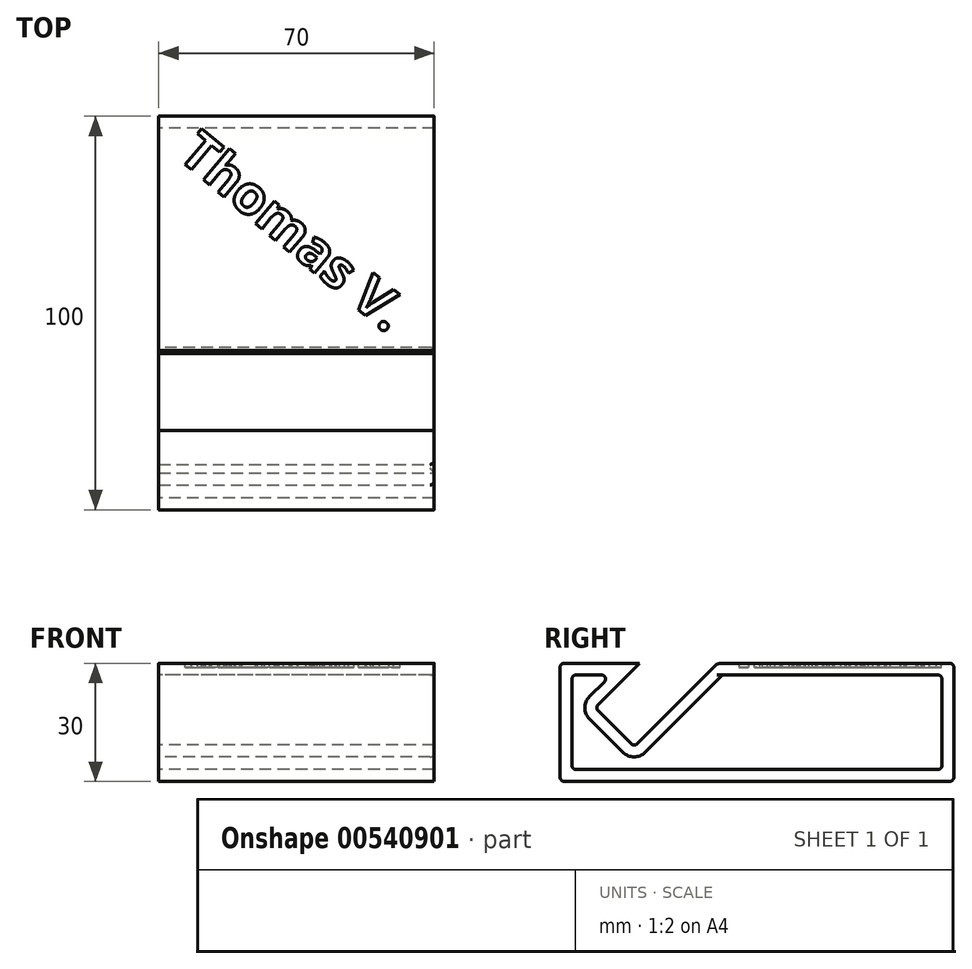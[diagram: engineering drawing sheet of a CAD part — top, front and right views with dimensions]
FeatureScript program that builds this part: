
annotation { "Feature Type Name" : "Feature", "Feature Type Description" : "" }
export const myFeature = defineFeature(function(context is Context, id is Id, definition is map)
    precondition{}
    {
        {
            var Q0;
            Q0=qCreatedBy(makeId("Top.planeOp"),FACE);
            var sketch = newSketch(context, id + "F0", { "sketchPlane" : qUnion([Q0])});
            skLineSegment(sketch, "E0.bottom", {"start": v(35, 50) * mm, "end": v(-35, 50) * mm});
            skLineSegment(sketch, "E0.top", {"start": v(35, -50) * mm, "end": v(-35, -50) * mm});
            skLineSegment(sketch, "E0.left", {"start": v(35, 50) * mm, "end": v(35, -50) * mm});
            skLineSegment(sketch, "E0.right", {"start": v(-35, 50) * mm, "end": v(-35, -50) * mm});
            skPoint(sketch, "E0.middle", {"position": v(0, 0) * mm});
            skSolve(sketch);
        }
        {
            var Q0;
            Q0 = qSketchRegion(id + "F0", true);
            extrude(context, id + "F1", {"entities" : qUnion([Q0]), "depth" : 30 * mm, "offsetDistance" : 25 * mm});
        }
        {
            var Q0;
            Q0=makeQuery(id+"F1.opExtrude","SWEPT_FACE",FACE,{"disambiguationData":[OSD([sQuery(id+"F0.wireOp",EDGE,"E0.left")])]});
            var sketch = newSketch(context, id + "F2", { "sketchPlane" : qUnion([Q0])});
            skLineSegment(sketch, "E1.bottom", {"start": v(-10, 30) * mm, "end": v(-31.21, 8.79) * mm});
            skLineSegment(sketch, "E1.top", {"start": v(-19.9, 39.9) * mm, "end": v(-41.11, 18.69) * mm});
            skLineSegment(sketch, "E1.left", {"start": v(-10, 30) * mm, "end": v(-19.9, 39.9) * mm});
            skLineSegment(sketch, "E1.right", {"start": v(-31.21, 8.79) * mm, "end": v(-41.11, 18.69) * mm});
            skPoint(sketch, "E2.firstSnap0", {"position": v(-20.6, 19.4) * mm});
            skSolve(sketch);
        }
        {
            var Q0;
            {var subQ0=sQuery(id+"F2.wireOp",EDGE,"E1.bottom");Q0=makeQuery(id+"F2.imprint","IMPRINT",FACE,{"disambiguationData":[TD([[makeQuery(id+"F2.imprint","IMPRINT",EDGE,{"derivedFrom":subQ0}),-1.0]])]});}
            extrude(context, id + "F3", {"entities" : qUnion([Q0]), "operationType" : NewBodyOperationType.REMOVE, "oppositeDirection" : true, "depth" : 146 * mm, "offsetDistance" : 25 * mm});
        }
        {
            var Q0;
            Q0=makeQuery(id+"F3.boolean.opBoolean","COPY",EDGE,{"derivedFrom":makeQuery(id+"F3.opExtrude","SWEPT_EDGE",EDGE,{"disambiguationData":[OSD([sQuery(id+"F0.wireOp",EDGE,"E0.left"),sQuery(id+"F2.wireOp",EDGE,"E1.top")])]})});
            var Q1;
            Q1=makeQuery(id+"F3.boolean.opBoolean","COPY",EDGE,{"derivedFrom":makeQuery(id+"F3.opExtrude","SWEPT_EDGE",EDGE,{"disambiguationData":[OSD([sQuery(id+"F2.wireOp",EDGE,"E1.top"),sQuery(id+"F2.wireOp",EDGE,"E1.right")])]})});
            var Q2;
            Q2=makeQuery(id+"F3.boolean.opBoolean","COPY",EDGE,{"derivedFrom":makeQuery(id+"F3.opExtrude","SWEPT_EDGE",EDGE,{"disambiguationData":[OSD([sQuery(id+"F2.wireOp",EDGE,"E1.bottom"),sQuery(id+"F2.wireOp",EDGE,"E1.right")])]})});
            fillet(context, id + "F4", {"entities" : qUnion([Q0, Q1, Q2]), "radius" : 1 * mm, "tangentPropagation" : true, "allowEdgeOverflow" : false});
        }
        {
            var Q0;
            Q0=makeQuery(id+"F3.boolean.opBoolean","COPY",EDGE,{"derivedFrom":makeQuery(id+"F3.opExtrude","SWEPT_EDGE",EDGE,{"disambiguationData":[OSD([sQuery(id+"F0.wireOp",EDGE,"E0.left"),sQuery(id+"F2.wireOp",EDGE,"E1.bottom"),sQuery(id+"F2.wireOp",EDGE,"E1.left")])]})});
            chamfer(context, id + "F5", {"entities" : qUnion([Q0]), "width" : 1 * mm, "tangentPropagation" : true});
        }
        {
            var Q0;
            Q0=makeQuery(id+"F1.opExtrude","SWEPT_FACE",FACE,{"disambiguationData":[OSD([sQuery(id+"F0.wireOp",EDGE,"E0.right")])]});
            var Q1;
            Q1=makeQuery(id+"F1.opExtrude","SWEPT_FACE",FACE,{"disambiguationData":[OSD([sQuery(id+"F0.wireOp",EDGE,"E0.left")])]});
            shell(context, id + "F6", {"entities" : qUnion([Q0, Q1]), "thickness" : 3 * mm});
        }
        {
            var Q0;
            {var subQ0=sQuery(id+"F0.wireOp",EDGE,"E0.bottom");var subQ1=sQuery(id+"F0.wireOp",EDGE,"E0.right");var subQ2=sQuery(id+"F0.wireOp",EDGE,"E0.left");Q0=makeQuery(id+"F3.boolean.opBoolean","SPLIT",FACE,{"disambiguationData":[TD([makeQuery(id+"F1.opExtrude","SWEPT_FACE",FACE,{"disambiguationData":[OSD([subQ0])]})])],"derivedFrom":makeQuery(id+"F1.opExtrude","CAP_FACE",FACE,{"disambiguationData":[OSD([subQ0,sQuery(id+"F0.wireOp",EDGE,"E0.top"),subQ2,subQ1])],"isStart":false})});}
            var sketch = newSketch(context, id + "F7", { "sketchPlane" : qUnion([Q0])});
            skText(sketch, "E3", { "text": "Thomas V.", "fontName": "OpenSans-Bold.ttf"});
            const initialGuessF7  = {"E3": [-0.0305, 0.0396, 0.76604, -0.64279, 0.0098]};
            skSetInitialGuess(sketch, initialGuessF7);
            skSolve(sketch);
        }
        {
            var Q0;
            Q0 = qSketchRegion(id + "F7", true);
            extrude(context, id + "F8", {"entities" : qUnion([Q0]), "operationType" : NewBodyOperationType.REMOVE, "oppositeDirection" : true, "depth" : 1 * mm, "offsetDistance" : 25 * mm});
        }
        {
            var Q0;
            Q0=makeQuery(id+"F1.opExtrude","CAP_EDGE",EDGE,{"disambiguationData":[OSD([sQuery(id+"F0.wireOp",EDGE,"E0.top")])],"isStart":false});
            var Q1;
            Q1=makeQuery(id+"F1.opExtrude","CAP_EDGE",EDGE,{"disambiguationData":[OSD([sQuery(id+"F0.wireOp",EDGE,"E0.top")])],"isStart":true});
            var Q2;
            Q2=makeQuery(id+"F1.opExtrude","CAP_EDGE",EDGE,{"disambiguationData":[OSD([sQuery(id+"F0.wireOp",EDGE,"E0.bottom")])],"isStart":true});
            var Q3;
            Q3=makeQuery(id+"F1.opExtrude","CAP_EDGE",EDGE,{"disambiguationData":[OSD([sQuery(id+"F0.wireOp",EDGE,"E0.bottom")])],"isStart":false});
            fillet(context, id + "F9", {"entities" : qUnion([Q0, Q1, Q2, Q3]), "radius" : 1 * mm, "tangentPropagation" : true, "allowEdgeOverflow" : false});
        }
        {
            var Q0;
            {var subQ0=sQuery(id+"F0.wireOp",EDGE,"E0.bottom");Q0=makeQuery(id+"F6.opShell","OFFSET_EDGE",EDGE,{"disambiguationData":[OSD([subQ0]),TDD([makeQuery(id+"F1.opExtrude","CAP_EDGE",EDGE,{"disambiguationData":[OSD([subQ0])],"isStart":false})])]});}
            var Q1;
            {var subQ0=sQuery(id+"F0.wireOp",EDGE,"E0.bottom");Q1=makeQuery(id+"F6.opShell","OFFSET_EDGE",EDGE,{"disambiguationData":[OSD([subQ0]),TDD([makeQuery(id+"F1.opExtrude","CAP_EDGE",EDGE,{"disambiguationData":[OSD([subQ0])],"isStart":true})])]});}
            var Q2;
            Q2=makeQuery(id+"F6.opShell","OFFSET_EDGE",EDGE,{"disambiguationData":[OSD([sQuery(id+"F0.wireOp",EDGE,"E0.bottom"),sQuery(id+"F0.wireOp",EDGE,"E0.top"),sQuery(id+"F0.wireOp",EDGE,"E0.left"),sQuery(id+"F0.wireOp",EDGE,"E0.right"),sQuery(id+"F2.wireOp",EDGE,"E1.top")])]});
            var Q3;
            {var subQ0=sQuery(id+"F0.wireOp",EDGE,"E0.top");Q3=makeQuery(id+"F6.opShell","OFFSET_EDGE",EDGE,{"disambiguationData":[OSD([subQ0]),TDD([makeQuery(id+"F1.opExtrude","CAP_EDGE",EDGE,{"disambiguationData":[OSD([subQ0])],"isStart":false})])]});}
            var Q4;
            {var subQ0=sQuery(id+"F0.wireOp",EDGE,"E0.top");Q4=makeQuery(id+"F6.opShell","OFFSET_EDGE",EDGE,{"disambiguationData":[OSD([subQ0]),TDD([makeQuery(id+"F1.opExtrude","CAP_EDGE",EDGE,{"disambiguationData":[OSD([subQ0])],"isStart":true})])]});}
            var Q5;
            {var subQ0=sQuery(id+"F2.wireOp",EDGE,"E1.bottom");var subQ1=sQuery(id+"F2.wireOp",EDGE,"E1.left");var subQ2=sQuery(id+"F0.wireOp",EDGE,"E0.left");Q5=makeQuery(id+"F6.opShell","OFFSET_EDGE",EDGE,{"disambiguationData":[OSD([subQ2,subQ0,subQ1]),TDD([makeQuery(id+"F5.opChamfer","BLEND_EDGE",EDGE,{"blendedFrom":[makeQuery(id+"F3.boolean.opBoolean","COPY",EDGE,{"derivedFrom":makeQuery(id+"F3.opExtrude","SWEPT_EDGE",EDGE,{"disambiguationData":[OSD([subQ2,subQ0,subQ1])]})}),makeQuery(id+"F3.boolean.opBoolean","COPY",FACE,{"derivedFrom":makeQuery(id+"F3.opExtrude","SWEPT_FACE",FACE,{"disambiguationData":[OSD([subQ0])]})})],"blendedInto":[makeQuery(id+"F3.boolean.opBoolean","COPY",FACE,{"derivedFrom":makeQuery(id+"F3.opExtrude","SWEPT_FACE",FACE,{"disambiguationData":[OSD([subQ0])]})})]})])]});}
            var Q6;
            Q6=makeQuery(id+"F6.opShell","OFFSET_EDGE",EDGE,{"disambiguationData":[OSD([sQuery(id+"F0.wireOp",EDGE,"E0.bottom"),sQuery(id+"F0.wireOp",EDGE,"E0.top"),sQuery(id+"F0.wireOp",EDGE,"E0.left"),sQuery(id+"F0.wireOp",EDGE,"E0.right"),sQuery(id+"F2.wireOp",EDGE,"E1.bottom"),sQuery(id+"F2.wireOp",EDGE,"E1.left")])]});
            fillet(context, id + "F10", {"entities" : qUnion([Q0, Q1, Q2, Q3, Q4, Q5, Q6]), "radius" : 1 * mm, "tangentPropagation" : true, "allowEdgeOverflow" : false});
        }
    });
